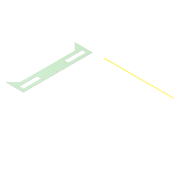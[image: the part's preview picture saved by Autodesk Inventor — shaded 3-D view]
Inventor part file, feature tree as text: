
AUTODESK INVENTOR PART (.ipt)
format: ipt  version: 2017 (Build 210142000, 142)  size: 1,104,384 bytes
history: native  units: mm
features: sketch x3, other x3, extrude x2, plane x1, hole x1, projected_geometry x1
ambient origin geometry x8: Origin, YZ Plane, XZ Plane, XY Plane, X Axis, Y Axis, Z Axis, Center Point
bodies: Solid1 (feature_tree)
feature tree (11):
  plane  "Work Plane1"
  extrude  "Extrusion1"  Depth=3.0mm TaperAngle=0.0deg
  extrude  "Extrusion2"  [1 undecoded]
  hole  "Hole1"  [1 undecoded]
  sketch  "Sketch1"  dims[d0=3.0mm d1=0.0mm d2=3.0mm d3=0.0mm]
  sketch  "Sketch2"  dims[d4=5.2mm d5=6.0mm d6=4.0mm d7=2.0mm d8=90.0deg d9=8.0mm d10=20.594885mm]
  sketch  "Sketch3"
  projected_geometry  "Projected Loop2"
  parser-record x1  (decoder bookkeeping rows leaked as tree rows — omitted from the tree; the rows remain in map.json)
  other  "Main assembly Test.iam"
  other  "3030 600mm_CPY:2"
note: 2 required parameter values undecoded (feature->parameter linkage not recoverable at this tier; creation-order binding heuristic only, values carry confidence <= 0.55)
note: 1 file-system path scrubbed to <path> (originals preserved in map.json)
